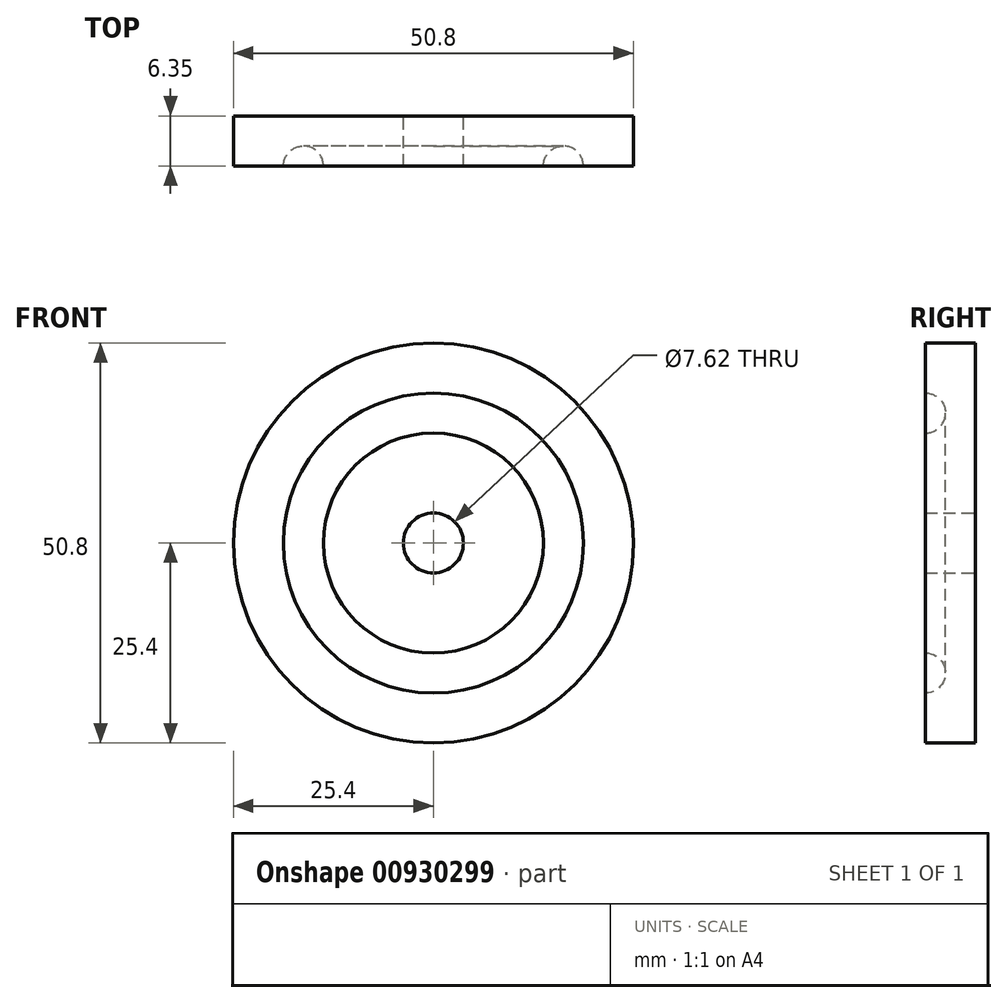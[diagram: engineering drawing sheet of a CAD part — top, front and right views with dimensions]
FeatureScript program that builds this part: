
annotation { "Feature Type Name" : "Feature", "Feature Type Description" : "" }
export const myFeature = defineFeature(function(context is Context, id is Id, definition is map)
    precondition{}
    {
        {
            var Q0;
            Q0=qCreatedBy(makeId("Front.planeOp"),FACE);
            var sketch = newSketch(context, id + "F0", { "sketchPlane" : qUnion([Q0])});
            skCircle(sketch, "E0", {"center": v(0, 0) * mm, "radius": 25.4 * mm});
            skCircle(sketch, "E1", {"center": v(0, 0) * mm, "radius": 3.81 * mm});
            skSolve(sketch);
        }
        {
            var Q0;
            Q0 = qSketchRegion(id + "F0", true);
            extrude(context, id + "F1", {"entities" : qUnion([Q0]), "depth" : 6.35 * mm, "offsetDistance" : 25.4 * mm});
        }
        {
            var Q0;
            Q0=makeQuery(id+"F1.opExtrude","CAP_FACE",FACE,{"disambiguationData":[OSD([sQuery(id+"F0.wireOp",EDGE,"E0"),sQuery(id+"F0.wireOp",EDGE,"E1")])],"isStart":false});
            var sketch = newSketch(context, id + "F2", { "sketchPlane" : qUnion([Q0])});
            skCircle(sketch, "E2", {"center": v(0, 0) * mm, "radius": 13.97 * mm});
            skCircle(sketch, "E3", {"center": v(0, 0) * mm, "radius": 19.05 * mm});
            skSolve(sketch);
        }
        {
            var Q0;
            Q0=makeQuery(id+"F2.imprint","IMPRINT",FACE,{"disambiguationData":[TD([[makeQuery(id+"F2.imprint","IMPRINT",EDGE,{"derivedFrom":sQuery(id+"F2.wireOp",EDGE,"E2")}),-1.0]])]});
            extrude(context, id + "F3", {"entities" : qUnion([Q0]), "operationType" : NewBodyOperationType.REMOVE, "oppositeDirection" : true, "depth" : 2.54 * mm, "offsetDistance" : 25.4 * mm});
        }
        {
            var Q0;
            Q0=makeQuery(id+"F3.boolean.opBoolean","COPY",EDGE,{"derivedFrom":makeQuery(id+"F3.opExtrude","CAP_EDGE",EDGE,{"disambiguationData":[OSD([sQuery(id+"F2.wireOp",EDGE,"E3")])],"isStart":false})});
            var Q1;
            Q1=makeQuery(id+"F3.boolean.opBoolean","COPY",EDGE,{"derivedFrom":makeQuery(id+"F3.opExtrude","CAP_EDGE",EDGE,{"disambiguationData":[OSD([sQuery(id+"F2.wireOp",EDGE,"E2")])],"isStart":false})});
            fillet(context, id + "F4", {"entities" : qUnion([Q0, Q1]), "tangentPropagation" : true, "radius" : 2.54 * mm, "defaultsChanged" : true, "vertexSettings" : [], "allowEdgeOverflow" : false});
        }
    });
